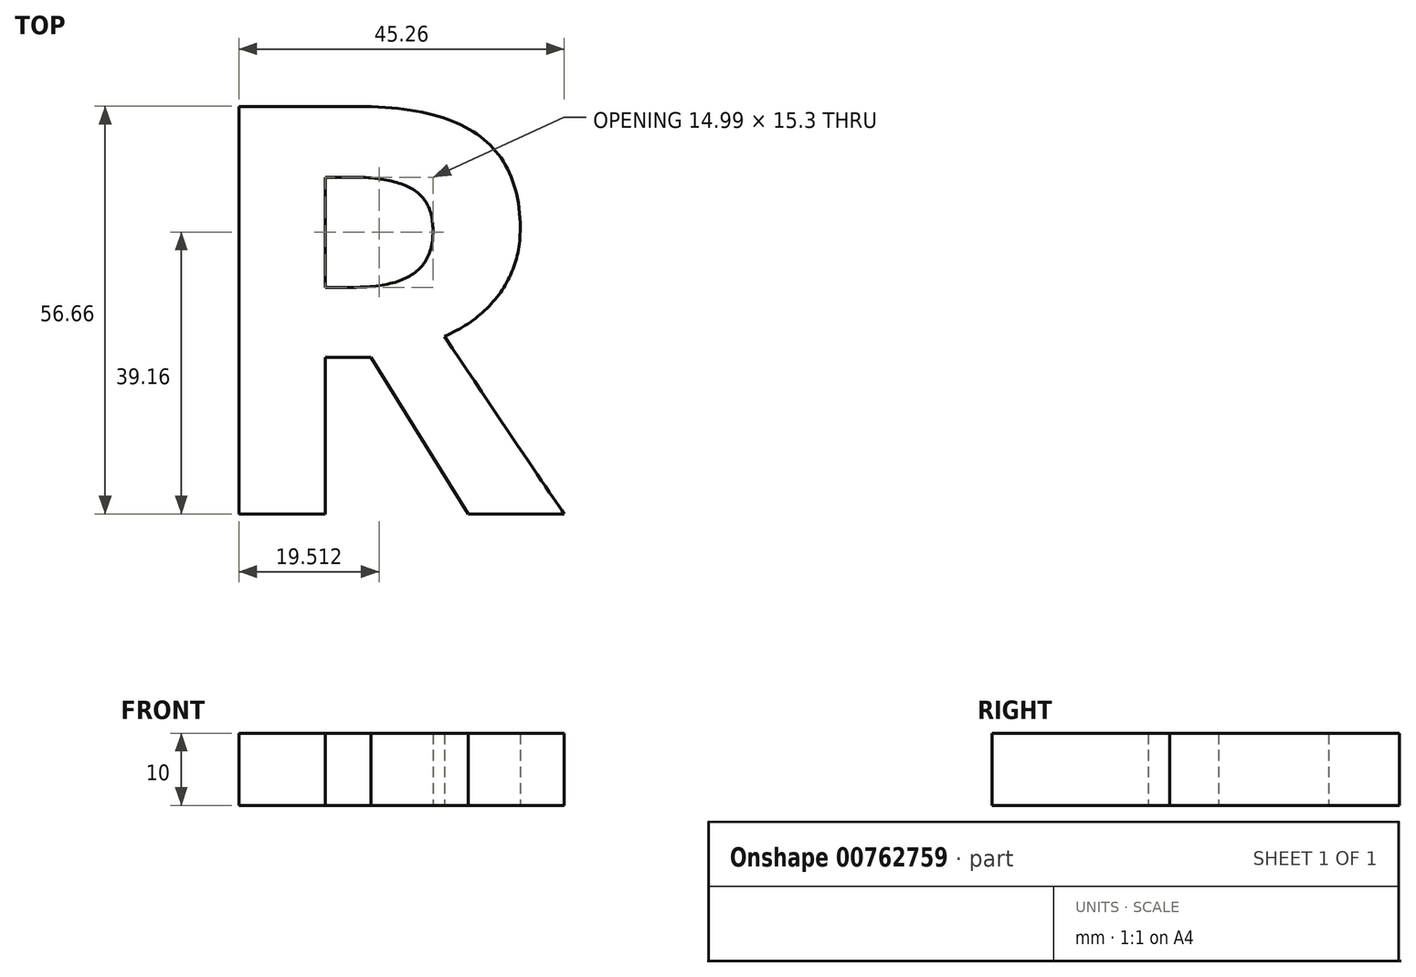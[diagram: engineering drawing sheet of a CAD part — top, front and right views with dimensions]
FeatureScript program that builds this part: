
annotation { "Feature Type Name" : "Feature", "Feature Type Description" : "" }
export const myFeature = defineFeature(function(context is Context, id is Id, definition is map)
    precondition{}
    {
        {
            var Q0;
            Q0=qCreatedBy(makeId("Top.planeOp"),FACE);
            var sketch = newSketch(context, id + "F0", { "sketchPlane" : qUnion([Q0])});
            skText(sketch, "E0", { "text": "R", "fontName": "OpenSans-Bold.ttf"});
            const initialGuessF0  = {"E0": [0, 0, 1, 0, 0.05714]};
            skSetInitialGuess(sketch, initialGuessF0);
            skSolve(sketch);
        }
        {
            var Q0;
            Q0 = qSketchRegion(id + "F0", true);
            extrude(context, id + "F1", {"entities" : qUnion([Q0]), "depth" : 10 * mm, "offsetDistance" : 25 * mm});
        }
    });
